# Revit family: HBLHA
name_source: partatom
category: Lighting Fixtures
units: mm (PartAtom-declared; Revit-internal decimal feet)

## family parameters
Cut with Voids When Loaded = No
Host = Face
Light Source = Yes
OmniClass Number = 23.80.70.14.14
OmniClass Title = Exterior Floodlights
Part Type = Normal
Room Calculation Point = No
Round Connector Dimension = Use Diameter
Shared = No

## types (1)
- HBLHA
    Apparent Load = 57 VA
    Application = Industrial, Warehouse, Refineries, Stell Mills, Chemical Plants
    Certification = UL1598A,Damp Listed,UL Sanitation certified per NSF standards,Wet Listed,NEMA 3,Class I Division 2,CSA,IP66
    Color Filter = 16777215
    Default Elevation = 48 "
    Description = The HBLH Series Hazardous LED Flood Light is designed to efficiently light classified areas in heavy industrial settings.
    Dimming Lamp Color Temperature Shift = <None>
    Dimming Protocol = 0-10V
    Emit Shape Visible in Rendering = No
    Emit from Circle Diameter = 11 "
    Environmental Conditions = Damp Location, Wet Location, Outdoor
    Fastners = Paint - Light Silver
    Features = High performance LED design delivering up to 100 Lumens per Watt
Specialized thermal management allows from -40˚C to 65˚C ambient temperature ratings
LED count ranges from 72 to 60 to 48 and all three LED counts are driven at 700 mA
Three distinct distributions: aisle, narrow and wide
5 available mounting options: Pendant, Ceiling, Wall, Stanchion, Cone
100,000 hours, long life at L70
Sealed optic for long life and durability
5000°K Color Temperature
< 70 CRI
CSA tested to UL1598 Wet Location
    Glass = Glass
    IP Rating = IP66
    Lamp = LED
    Load Classification = Lighting
    Manufacturer = Columbia Lighting
    Material Finish = Paint - White Texture
    Model = HBLHA
    Mounting Type = Pendant, Stanchion, Ceiling, Wall, Cone
    Optics = Narrow
    Photometric Web File = HBL-48LU-5K-A-070.ies
    Power Factor = 1
    Tilt Angle = -90.00°
    URL = https://www.currentlighting.com
    Voltage = 120 V
    Warranty = 5 Year Warranty
    Watt = 57 W
    Wattage Comments = 57 Watts, 24 LEDs

## geometry (parser evidence)
native form markers: Blend x4, Sweep x5
no freeform markers — native parametric forms only
